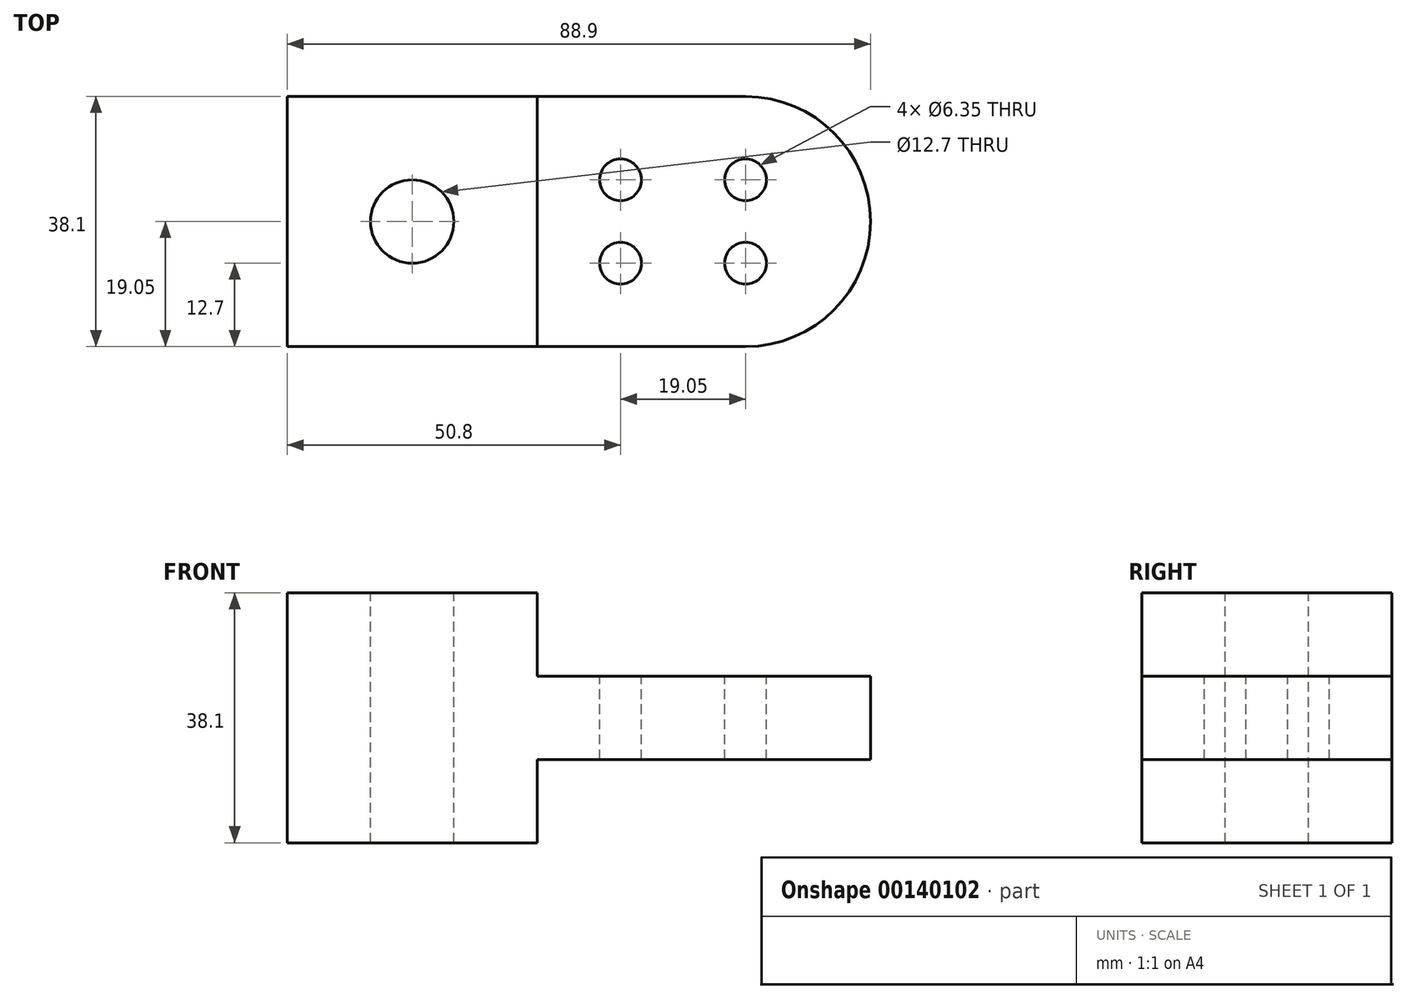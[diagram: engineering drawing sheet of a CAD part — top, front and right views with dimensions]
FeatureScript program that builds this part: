
annotation { "Feature Type Name" : "Feature", "Feature Type Description" : "" }
export const myFeature = defineFeature(function(context is Context, id is Id, definition is map)
    precondition{}
    {
        {
            var Q0;
            Q0=qCreatedBy(makeId("Top.planeOp"),FACE);
            var sketch = newSketch(context, id + "F0", { "sketchPlane" : qUnion([Q0])});
            skLineSegment(sketch, "E0.bottom", {"start": v(0, 0) * mm, "end": v(88.9, 0) * mm});
            skLineSegment(sketch, "E0.top", {"start": v(0, 38.1) * mm, "end": v(88.9, 38.1) * mm});
            skLineSegment(sketch, "E0.left", {"start": v(0, 0) * mm, "end": v(0, 38.1) * mm});
            skLineSegment(sketch, "E0.right", {"start": v(88.9, 0) * mm, "end": v(88.9, 38.1) * mm});
            skArc(sketch, "E1", {"start": v(69.85, 0) * mm, "mid": v(88.9, 19.05) * mm, "end": v(69.85, 38.1) * mm});
            skLineSegment(sketch, "E2", {"start": v(38.1, 38.1) * mm, "end": v(38.1, 0) * mm});
            skSolve(sketch);
        }
        {
            var Q0;
            {var subQ0=sQuery(id+"F0.wireOp",EDGE,"E0.left");Q0=makeQuery(id+"F0.imprint","IMPRINT",FACE,{"disambiguationData":[TD([[makeQuery(id+"F0.imprint","IMPRINT",EDGE,{"derivedFrom":subQ0}),-1.0]])]});}
            var Q1;
            {var subQ6=sQuery(id+"F0.wireOp",EDGE,"E2");Q1=makeQuery(id+"F0.imprint","IMPRINT",FACE,{"disambiguationData":[TD([[makeQuery(id+"F0.imprint","IMPRINT",EDGE,{"derivedFrom":subQ6}),1.0]])]});}
            extrude(context, id + "F1", {"entities" : qUnion([Q0, Q1]), "depth" : 38.1 * mm});
        }
        {
            var Q0;
            Q0=qCreatedBy(makeId("Front.planeOp"),FACE);
            var sketch = newSketch(context, id + "F2", { "sketchPlane" : qUnion([Q0])});
            skLineSegment(sketch, "E3", {"start": v(38.1, 38.1) * mm, "end": v(38.1, 0) * mm});
            skLineSegment(sketch, "E4", {"start": v(38.1, 38.1) * mm, "end": v(88.9, 38.1) * mm});
            skLineSegment(sketch, "E5", {"start": v(88.9, 38.1) * mm, "end": v(88.9, 25.4) * mm});
            skLineSegment(sketch, "E6", {"start": v(88.9, 25.4) * mm, "end": v(38.1, 25.4) * mm});
            skLineSegment(sketch, "E7", {"start": v(38.1, 38.1) * mm, "end": v(38.1, 25.4) * mm});
            skLineSegment(sketch, "E8", {"start": v(38.1, 0) * mm, "end": v(88.9, 0) * mm});
            skLineSegment(sketch, "E9", {"start": v(88.9, 0) * mm, "end": v(88.9, 12.7) * mm});
            skLineSegment(sketch, "E10", {"start": v(88.9, 12.7) * mm, "end": v(38.1, 12.7) * mm});
            skLineSegment(sketch, "E11", {"start": v(38.1, 12.7) * mm, "end": v(38.1, 0) * mm});
            skSolve(sketch);
        }
        {
            var Q0;
            Q0 = qSketchRegion(id + "F2", true);
            extrude(context, id + "F3", {"entities" : qUnion([Q0]), "operationType" : NewBodyOperationType.REMOVE, "endBound" : BoundingType.THROUGH_ALL, "oppositeDirection" : true, "depth" : 25.4 * mm});
        }
        {
            var Q0;
            Q0=makeQuery(id+"F1.opExtrude","CAP_FACE",FACE,{"disambiguationData":[OSD([sQuery(id+"F0.wireOp",EDGE,"E0.bottom"),sQuery(id+"F0.wireOp",EDGE,"E0.top"),sQuery(id+"F0.wireOp",EDGE,"E0.left"),sQuery(id+"F0.wireOp",EDGE,"E1")])],"isStart":false});
            var sketch = newSketch(context, id + "F4", { "sketchPlane" : qUnion([Q0])});
            skCircle(sketch, "E12", {"center": v(19.05, 19.05) * mm, "radius": 6.35 * mm});
            skPoint(sketch, "E12.centerSnap0", {"position": v(0, 19.05) * mm});
            skSolve(sketch);
        }
        {
            var Q0;
            Q0 = qSketchRegion(id + "F4", true);
            extrude(context, id + "F5", {"entities" : qUnion([Q0]), "operationType" : NewBodyOperationType.REMOVE, "endBound" : BoundingType.THROUGH_ALL, "oppositeDirection" : true, "depth" : 25.4 * mm});
        }
        {
            var Q0;
            Q0=makeQuery(id+"F3.boolean.opBoolean","COPY",FACE,{"derivedFrom":makeQuery(id+"F3.opExtrude","SWEPT_FACE",FACE,{"disambiguationData":[OSD([sQuery(id+"F2.wireOp",EDGE,"E6")])]})});
            var sketch = newSketch(context, id + "F6", { "sketchPlane" : qUnion([Q0])});
            skCircle(sketch, "E13", {"center": v(50.8, 25.4) * mm, "radius": 3.18 * mm});
            skCircle(sketch, "E14", {"center": v(50.8, 12.7) * mm, "radius": 3.18 * mm});
            skCircle(sketch, "E15", {"center": v(69.85, 25.4) * mm, "radius": 3.18 * mm});
            skCircle(sketch, "E16", {"center": v(69.85, 12.7) * mm, "radius": 3.18 * mm});
            skLineSegment(sketch, "E17", {"start": v(50.8, 38.1) * mm, "end": v(50.8, 0) * mm, "construction": true});
            skLineSegment(sketch, "E18", {"start": v(69.85, 38.1) * mm, "end": v(69.85, 0) * mm, "construction": true});
            skSolve(sketch);
        }
        {
            var Q0;
            Q0 = qSketchRegion(id + "F6", true);
            extrude(context, id + "F7", {"entities" : qUnion([Q0]), "operationType" : NewBodyOperationType.REMOVE, "endBound" : BoundingType.THROUGH_ALL, "oppositeDirection" : true, "depth" : 25.4 * mm});
        }
    });
